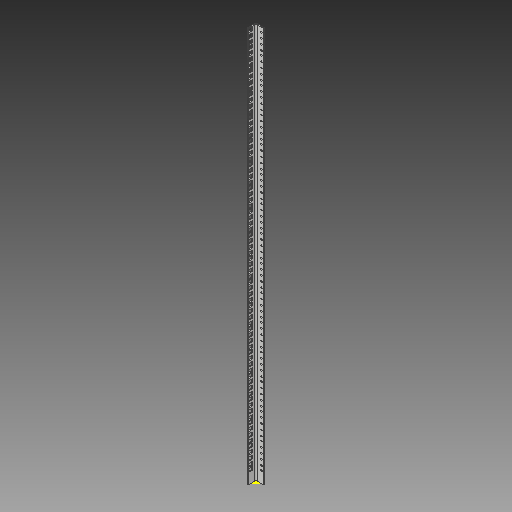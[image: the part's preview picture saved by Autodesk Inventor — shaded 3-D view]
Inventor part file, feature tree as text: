
AUTODESK INVENTOR PART (.ipt)
format: ipt  version: 2017 (Build 210142000, 142)  size: 429,568 bytes
history: native  units: in
note: dims shown in document units (in); Inventor stores cm internally (conversion verified against a paired STEP export)
features: sketch x4, sheet_metal_op x3, extrude x2, pattern_linear x2, other x2
ambient origin geometry x8: Origin, YZ Plane, XZ Plane, XY Plane, X Axis, Y Axis, Z Axis, Center Point
bodies: Solid1 (feature_tree)
feature tree (13):
  sheet_metal_op  "Contour Flange1"
  extrude  "Extrusion1"  Depth=1.0in
  pattern_linear  "Rectangular Pattern1"  Spacing1=0.12in  [1 undecoded]
  sketch  "Sketch3"  dims[d4=0.06in]
  sketch  "Sketch4"  dims[d5=0.24in d6=0.12in d7=46.25in d8=0.12in d9=0.12in d10=0.48in d11=0.12in d12=0.12in d13=0.25in d14=0.25in d15=0.3937in d16=0.3937in d17=0.626in d18=0.3937in d19=0.3937in d20=0.626in d21=0.3937in d22=0.3937in d23=0.5in d24=0.3937in d25=0.3937in d26=0.2362in d27=0.0in d28=7.4803in d30=2.378in d31=0.1902in d32=0.5in d33=0.25in d34=0.1902in d35=0.626in d36=0.25in d37=0.1902in d38=0.626in d39=0.1902in d40=0.626in d41=0.1902in d42=0.5in d43=0.3937in d44=0.0in d45=5.9055in d47=3.0039in]
  extrude  "Extrusion2"  Depth=46.25in
  pattern_linear  "Rectangular Pattern2"  Spacing1=0.12in  [1 undecoded]
  sketch  "Sketch1"  dims[d0=1.0in d1=1.0in]
  other  "Plate1"
  sheet_metal_op  "Bend1"
  sheet_metal_op  "Corner1"
  sketch  "Sketch2"  dims[d3=0.12in]
  other  "10-32 holes"
note: 2 required parameter values undecoded (feature->parameter linkage not recoverable at this tier; creation-order binding heuristic only, values carry confidence <= 0.55)
